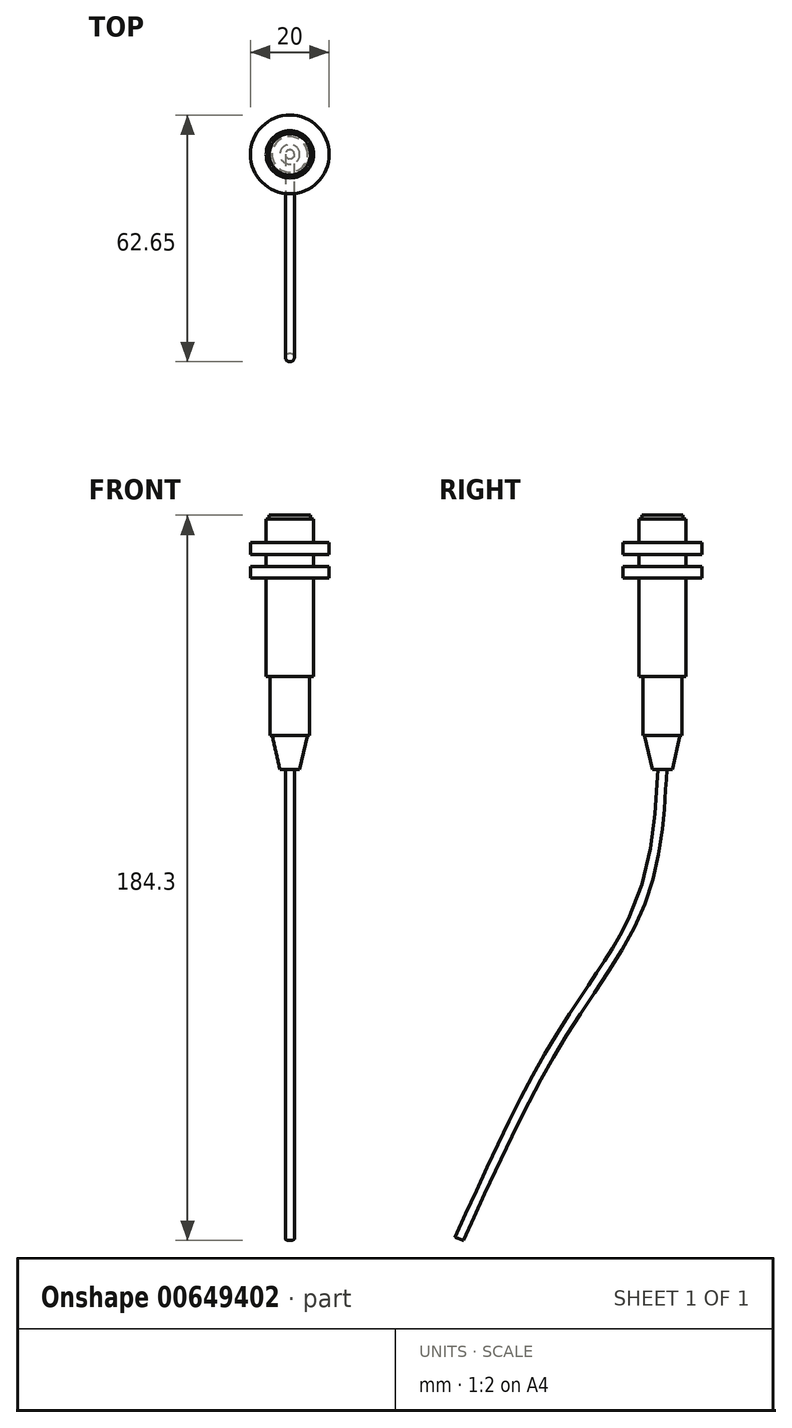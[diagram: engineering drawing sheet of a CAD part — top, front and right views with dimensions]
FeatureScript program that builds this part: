
annotation { "Feature Type Name" : "Feature", "Feature Type Description" : "" }
export const myFeature = defineFeature(function(context is Context, id is Id, definition is map)
    precondition{}
    {
        {
            var Q0;
            Q0=qCreatedBy(makeId("Front.planeOp"),FACE);
            var sketch = newSketch(context, id + "F0", { "sketchPlane" : qUnion([Q0])});
            skLineSegment(sketch, "E0.bottom", {"start": v(0, 0) * mm, "end": v(5, 0) * mm});
            skLineSegment(sketch, "E0.top", {"start": v(0, 15) * mm, "end": v(5, 15) * mm});
            skLineSegment(sketch, "E0.left", {"start": v(0, 0) * mm, "end": v(0, 15) * mm});
            skLineSegment(sketch, "E0.right", {"start": v(5, 0) * mm, "end": v(5, 15) * mm});
            skLineSegment(sketch, "E1.bottom", {"start": v(0, 15) * mm, "end": v(6, 15) * mm});
            skLineSegment(sketch, "E1.top", {"start": v(0, 55) * mm, "end": v(6, 55) * mm});
            skLineSegment(sketch, "E1.left", {"start": v(0, 15) * mm, "end": v(0, 55) * mm});
            skLineSegment(sketch, "E1.right", {"start": v(6, 15) * mm, "end": v(6, 55) * mm});
            skLineSegment(sketch, "E2", {"start": v(0, 0) * mm, "end": v(0, -8.6) * mm});
            skLineSegment(sketch, "E3", {"start": v(0, -8.6) * mm, "end": v(2.52, -8.6) * mm});
            skLineSegment(sketch, "E4", {"start": v(2.52, -8.6) * mm, "end": v(4.5, 0) * mm});
            skLineSegment(sketch, "E5.bottom", {"start": v(0, 55) * mm, "end": v(5.25, 55) * mm});
            skLineSegment(sketch, "E5.top", {"start": v(0, 56) * mm, "end": v(5.25, 56) * mm});
            skLineSegment(sketch, "E5.left", {"start": v(0, 55) * mm, "end": v(0, 56) * mm});
            skLineSegment(sketch, "E5.right", {"start": v(5.25, 55) * mm, "end": v(5.25, 56) * mm});
            skLineSegment(sketch, "E6.bottom", {"start": v(6, 49) * mm, "end": v(10, 49) * mm});
            skLineSegment(sketch, "E6.top", {"start": v(6, 46) * mm, "end": v(10, 46) * mm});
            skLineSegment(sketch, "E6.left", {"start": v(6, 49) * mm, "end": v(6, 46) * mm});
            skLineSegment(sketch, "E6.right", {"start": v(10, 49) * mm, "end": v(10, 46) * mm});
            skLineSegment(sketch, "E7.bottom", {"start": v(6, 43) * mm, "end": v(10, 43) * mm});
            skLineSegment(sketch, "E7.top", {"start": v(6, 40) * mm, "end": v(10, 40) * mm});
            skLineSegment(sketch, "E7.left", {"start": v(6, 43) * mm, "end": v(6, 40) * mm});
            skLineSegment(sketch, "E7.right", {"start": v(10, 43) * mm, "end": v(10, 40) * mm});
            skSolve(sketch);
        }
        {
            var Q0;
            Q0 = qSketchRegion(id + "F0", true);
            var Q1;
            Q1=sQuery(id+"F0.wireOp",EDGE,"E1.left");
            revolve(context, id + "F1", {"entities" : qUnion([Q0]), "axis" : qUnion([Q1]), "revolveType" : RevolveType.FULL});
        }
        {
            var Q0;
            Q0=makeQuery(id+"F1.opRevolve","SWEPT_FACE",FACE,{"disambiguationData":[OSD([sQuery(id+"F0.wireOp",EDGE,"E3")])]});
            var sketch = newSketch(context, id + "F2", { "sketchPlane" : qUnion([Q0])});
            skCircle(sketch, "E8", {"center": v(0, 0) * mm, "radius": 1.15 * mm});
            skSolve(sketch);
        }
        {
            var Q0;
            Q0=qCreatedBy(makeId("Right.planeOp"),FACE);
            var sketch = newSketch(context, id + "F3", { "sketchPlane" : qUnion([Q0])});
            skPoint(sketch, "E9.0", {"position": v(0, -8.6) * mm});
            skFitSpline(sketch, "E10", {"points": [v(0, -8.6) * mm, v(-5.45, -42.24) * mm, v(-26.11, -76.88) * mm, v(-51.58, -127.89) * mm], "startDerivative": vector(-6.91, -116.8) * mm, "endDerivative": vector(-63.82, -141.21) * mm});
            skSolve(sketch);
        }
        {
            var Q0;
            Q0 = qSketchRegion(id + "F2", true);
            var Q1;
            Q1 = qConstructionFilter(qBodyType(qCreatedBy(id + "F3" ,EDGE), BodyType.WIRE), ConstructionObject.NO);
            sweep(context, id + "F4", {"operationType" : NewBodyOperationType.ADD, "profiles" : qUnion([Q0]), "path" : qUnion([Q1])});
        }
    });
